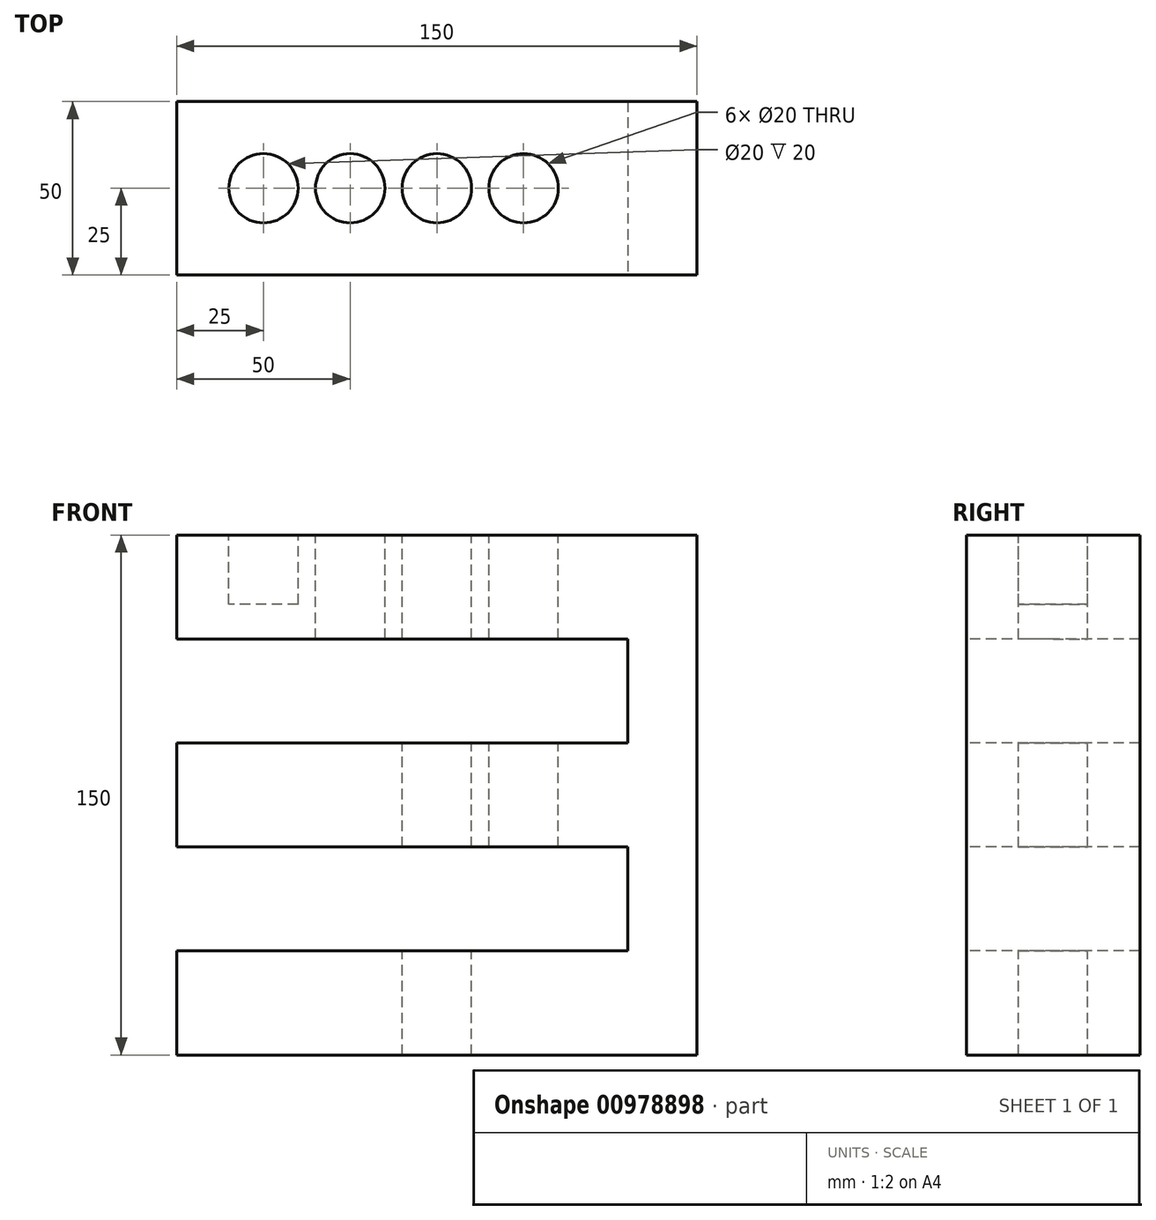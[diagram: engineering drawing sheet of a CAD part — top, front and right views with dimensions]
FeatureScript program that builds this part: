
annotation { "Feature Type Name" : "Feature", "Feature Type Description" : "" }
export const myFeature = defineFeature(function(context is Context, id is Id, definition is map)
    precondition{}
    {
        {
            var Q0;
            Q0=qCreatedBy(makeId("Front.planeOp"),FACE);
            var sketch = newSketch(context, id + "F0", { "sketchPlane" : qUnion([Q0])});
            skLineSegment(sketch, "E0.bottom", {"start": v(0, 0) * mm, "end": v(150, 0) * mm});
            skLineSegment(sketch, "E0.top", {"start": v(0, -150) * mm, "end": v(150, -150) * mm});
            skLineSegment(sketch, "E0.left", {"start": v(0, 0) * mm, "end": v(0, -30) * mm});
            skLineSegment(sketch, "E0.right", {"start": v(150, 0) * mm, "end": v(150, -150) * mm});
            skLineSegment(sketch, "E1.bottom", {"start": v(0, -30) * mm, "end": v(130, -30) * mm});
            skLineSegment(sketch, "E1.top", {"start": v(0, -60) * mm, "end": v(130, -60) * mm});
            skLineSegment(sketch, "E1.right", {"start": v(130, -30) * mm, "end": v(130, -60) * mm});
            skLineSegment(sketch, "E2.bottom", {"start": v(0, -90) * mm, "end": v(130, -90) * mm});
            skLineSegment(sketch, "E2.top", {"start": v(0, -120) * mm, "end": v(130, -120) * mm});
            skLineSegment(sketch, "E2.right", {"start": v(130, -90) * mm, "end": v(130, -120) * mm});
            skLineSegment(sketch, "E3.trimOffspring", {"start": v(0, -60) * mm, "end": v(0, -90) * mm});
            skLineSegment(sketch, "E4.trimOffspring", {"start": v(0, -120) * mm, "end": v(0, -150) * mm});
            skSolve(sketch);
        }
        {
            var Q0;
            Q0=makeQuery(id+"F0.imprint","IMPRINT",FACE,{"disambiguationData":[TD([[makeQuery(id+"F0.imprint","IMPRINT",EDGE,{"derivedFrom":sQuery(id+"F0.wireOp",EDGE,"E0.bottom")}),-1.0]])]});
            extrude(context, id + "F1", {"entities" : qUnion([Q0]), "oppositeDirection" : true, "depth" : 50 * mm, "offsetDistance" : 25 * mm});
        }
        {
            var Q0;
            Q0=makeQuery(id+"F1.opExtrude","SWEPT_EDGE",EDGE,{"disambiguationData":[OSD([sQuery(id+"F0.wireOp",EDGE,"E0.bottom"),sQuery(id+"F0.wireOp",EDGE,"E0.left")])]});
            cPoint(context, id + "F2", {"entities" : qUnion([Q0]), "parameter" : 0.5});
        }
        {
            var Q0;
            Q0=qCreatedBy(makeId("Front.planeOp"),FACE);
            var Q1;
            Q1 = qCreatedBy(id + "F2" ,VERTEX);
            cPlane(context, id + "F3", {"entities" : qUnion([Q0, Q1]), "cplaneType" : CPlaneType.PLANE_POINT, "offset" : 25 * mm, "width" : 150 * mm, "height" : 150 * mm});
        }
        {
            var Q0;
            Q0=qCreatedBy(makeId("Top.planeOp"),FACE);
            var sketch = newSketch(context, id + "F4", { "sketchPlane" : qUnion([Q0])});
            skCircle(sketch, "E5", {"center": v(25, 25) * mm, "radius": 10 * mm});
            skCircle(sketch, "E6", {"center": v(50, 25) * mm, "radius": 10 * mm});
            skCircle(sketch, "E7", {"center": v(75, 25) * mm, "radius": 10 * mm});
            skCircle(sketch, "E8", {"center": v(100, 25) * mm, "radius": 10 * mm});
            skSolve(sketch);
        }
        {
            var Q0;
            Q0=makeQuery(id+"F4.imprint","IMPRINT",FACE,{"disambiguationData":[TD([[makeQuery(id+"F4.imprint","IMPRINT",EDGE,{"derivedFrom":sQuery(id+"F4.wireOp",EDGE,"E5")}),1.0]])]});
            extrude(context, id + "F5", {"entities" : qUnion([Q0]), "operationType" : NewBodyOperationType.REMOVE, "oppositeDirection" : true, "depth" : 20 * mm, "offsetDistance" : 25 * mm});
        }
        {
            var Q0;
            Q0=makeQuery(id+"F4.imprint","IMPRINT",FACE,{"disambiguationData":[TD([[makeQuery(id+"F4.imprint","IMPRINT",EDGE,{"derivedFrom":sQuery(id+"F4.wireOp",EDGE,"E6")}),1.0]])]});
            var Q1;
            Q1=makeQuery(id+"F1.opExtrude","SWEPT_FACE",FACE,{"disambiguationData":[OSD([sQuery(id+"F0.wireOp",EDGE,"E1.bottom")])]});
            extrude(context, id + "F6", {"entities" : qUnion([Q0]), "operationType" : NewBodyOperationType.REMOVE, "endBound" : BoundingType.UP_TO_SURFACE, "oppositeDirection" : true, "depth" : 25 * mm, "endBoundEntityFace" : qUnion([Q1]), "offsetDistance" : 25 * mm});
        }
        {
            var Q0;
            Q0=makeQuery(id+"F4.imprint","IMPRINT",FACE,{"disambiguationData":[TD([[makeQuery(id+"F4.imprint","IMPRINT",EDGE,{"derivedFrom":sQuery(id+"F4.wireOp",EDGE,"E7")}),1.0]])]});
            extrude(context, id + "F7", {"entities" : qUnion([Q0]), "operationType" : NewBodyOperationType.REMOVE, "endBound" : BoundingType.THROUGH_ALL, "oppositeDirection" : true, "depth" : 25 * mm, "offsetDistance" : 25 * mm});
        }
        {
            var Q0;
            Q0=makeQuery(id+"F4.imprint","IMPRINT",FACE,{"disambiguationData":[TD([[makeQuery(id+"F4.imprint","IMPRINT",EDGE,{"derivedFrom":sQuery(id+"F4.wireOp",EDGE,"E8")}),1.0]])]});
            var Q1;
            Q1=makeQuery(id+"F1.opExtrude","SWEPT_FACE",FACE,{"disambiguationData":[OSD([sQuery(id+"F0.wireOp",EDGE,"E2.bottom")])]});
            extrude(context, id + "F8", {"entities" : qUnion([Q0]), "operationType" : NewBodyOperationType.REMOVE, "endBound" : BoundingType.UP_TO_SURFACE, "oppositeDirection" : true, "depth" : 25 * mm, "endBoundEntityFace" : qUnion([Q1]), "offsetDistance" : 25 * mm});
        }
    });
